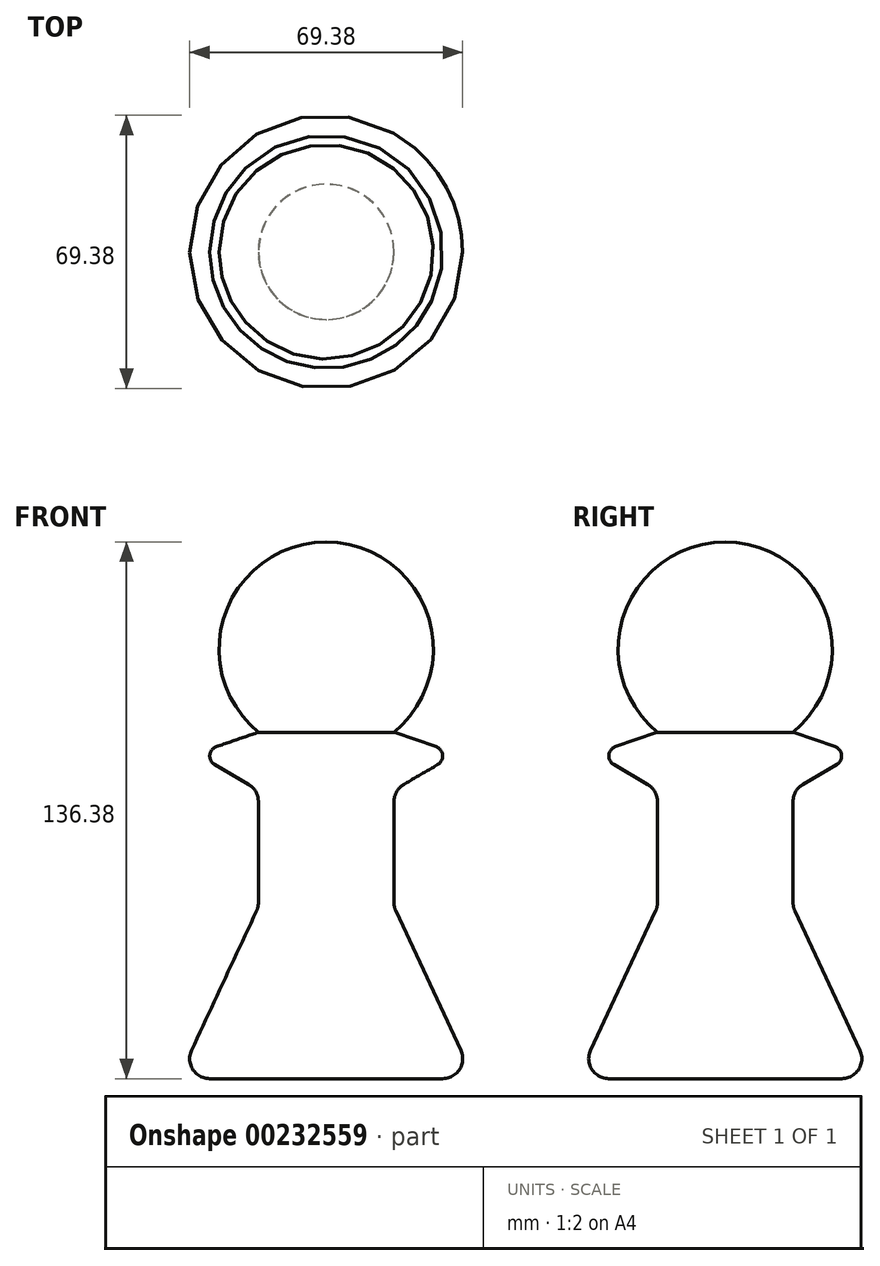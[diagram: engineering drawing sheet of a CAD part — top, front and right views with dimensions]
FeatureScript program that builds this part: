
annotation { "Feature Type Name" : "Feature", "Feature Type Description" : "" }
export const myFeature = defineFeature(function(context is Context, id is Id, definition is map)
    precondition{}
    {
        {
            var Q0;
            Q0=qCreatedBy(makeId("Right.planeOp"),FACE);
            var sketch = newSketch(context, id + "F0", { "sketchPlane" : qUnion([Q0])});
            skLineSegment(sketch, "E0.right", {"start": v(17.23, 14.67) * mm, "end": v(17.23, -73.33) * mm});
            skPoint(sketch, "E1", {"position": v(17.23, -29.74) * mm});
            skPoint(sketch, "E2", {"position": v(17.23, 14.67) * mm});
            skLineSegment(sketch, "E3", {"start": v(17.23, -73.33) * mm, "end": v(37.58, -73.33) * mm});
            skLineSegment(sketch, "E4", {"start": v(17.23, -29.74) * mm, "end": v(37.58, -73.33) * mm});
            skLineSegment(sketch, "E5", {"start": v(17.23, 14.67) * mm, "end": v(33.14, 9.26) * mm});
            skLineSegment(sketch, "E6", {"start": v(33.14, 9.26) * mm, "end": v(17.23, 0) * mm});
            skLineSegment(sketch, "E7", {"start": v(0, 63.05) * mm, "end": v(0, -73.33) * mm});
            skArc(sketch, "E8", {"start": v(0, 8.54) * mm, "mid": v(27.22, 35.8) * mm, "end": v(0, 63.05) * mm});
            skLineSegment(sketch, "E9.bottom", {"start": v(0, 14.67) * mm, "end": v(17.23, 14.67) * mm});
            skLineSegment(sketch, "E9.top", {"start": v(0, -73.33) * mm, "end": v(17.23, -73.33) * mm});
            skLineSegment(sketch, "E9.left", {"start": v(0, 14.67) * mm, "end": v(0, -73.33) * mm});
            skSolve(sketch);
        }
        {
            var Q0;
            {var subQ0=sQuery(id+"F0.wireOp",EDGE,"E3");Q0=makeQuery(id+"F0.imprint","IMPRINT",FACE,{"disambiguationData":[TD([[makeQuery(id+"F0.imprint","IMPRINT",EDGE,{"derivedFrom":subQ0}),1.0]])]});}
            var Q1;
            {var subQ0=sQuery(id+"F0.wireOp",EDGE,"E5");Q1=makeQuery(id+"F0.imprint","IMPRINT",FACE,{"disambiguationData":[TD([[makeQuery(id+"F0.imprint","IMPRINT",EDGE,{"derivedFrom":subQ0}),-1.0]])]});}
            var Q2;
            {var subQ0=sQuery(id+"F0.wireOp",EDGE,"E9.left");var subQ1=sQuery(id+"F0.wireOp",EDGE,"E8");var subQ2=makeQuery(id+"F0.imprint","INTERSECT",VERTEX,{"derivedFrom":[subQ1,subQ0]});Q2=makeQuery(id+"F0.imprint","IMPRINT",FACE,{"disambiguationData":[TD([[makeQuery(id+"F0.imprint","IMPRINT",EDGE,{"disambiguationData":[TD([[subQ2,-1.0]])],"derivedFrom":subQ1}),1.0]])]});}
            var Q3;
            {var subQ3=sQuery(id+"F0.wireOp",EDGE,"E9.top");Q3=makeQuery(id+"F0.imprint","IMPRINT",FACE,{"disambiguationData":[TD([[makeQuery(id+"F0.imprint","IMPRINT",EDGE,{"derivedFrom":subQ3}),1.0]])]});}
            var Q4;
            {var subQ0=sQuery(id+"F0.wireOp",EDGE,"E7");Q4=makeQuery(id+"F0.imprint","IMPRINT",FACE,{"disambiguationData":[TD([[makeQuery(id+"F0.imprint","IMPRINT",EDGE,{"derivedFrom":subQ0}),1.0]])]});}
            var Q5;
            Q5=sQuery(id+"F0.wireOp",EDGE,"E7");
            revolve(context, id + "F1", {"entities" : qUnion([Q0, Q1, Q2, Q3, Q4]), "axis" : qUnion([Q5]), "revolveType" : RevolveType.FULL});
        }
        {
            var Q0;
            Q0=makeQuery(id+"F1.opRevolve","SWEPT_EDGE",EDGE,{"disambiguationData":[OSD([sQuery(id+"F0.wireOp",EDGE,"E5"),sQuery(id+"F0.wireOp",EDGE,"E6")])]});
            fillet(context, id + "F2", {"entities" : qUnion([Q0]), "radius" : 2.54 * mm, "tangentPropagation" : true, "allowEdgeOverflow" : false});
        }
        {
            var Q0;
            Q0=makeQuery(id+"F1.opRevolve","SWEPT_EDGE",EDGE,{"disambiguationData":[OSD([sQuery(id+"F0.wireOp",EDGE,"E5"),sQuery(id+"F0.wireOp",EDGE,"E9.bottom"),sQuery(id+"F0.wireOp",EDGE,"E0.right")])]});
            fillet(context, id + "F3", {"entities" : qUnion([Q0]), "radius" : 5.08 * mm, "tangentPropagation" : true, "allowEdgeOverflow" : false});
        }
        {
            var Q0;
            {var subQ0=sQuery(id+"F0.wireOp",EDGE,"E5");Q0=makeQuery(id+"F3.opFillet","BLEND_EDGE",EDGE,{"blendedFrom":[makeQuery(id+"F1.opRevolve","SWEPT_EDGE",EDGE,{"disambiguationData":[OSD([subQ0,sQuery(id+"F0.wireOp",EDGE,"E9.bottom"),sQuery(id+"F0.wireOp",EDGE,"E0.right")])]}),makeQuery(id+"F1.opRevolve","SWEPT_FACE",FACE,{"disambiguationData":[OSD([subQ0])]})],"blendedInto":[makeQuery(id+"F1.opRevolve","SWEPT_FACE",FACE,{"disambiguationData":[OSD([subQ0])]})]});}
            var Q1;
            Q1=makeQuery(id+"F1.opRevolve","SWEPT_FACE",FACE,{"disambiguationData":[OSD([sQuery(id+"F0.wireOp",EDGE,"E6")])]});
            var Q2;
            Q2=makeQuery(id+"F1.opRevolve","SWEPT_EDGE",EDGE,{"disambiguationData":[OSD([sQuery(id+"F0.wireOp",EDGE,"E4"),sQuery(id+"F0.wireOp",EDGE,"E0.right")])]});
            var Q3;
            Q3=makeQuery(id+"F1.opRevolve","SWEPT_FACE",FACE,{"disambiguationData":[OSD([sQuery(id+"F0.wireOp",EDGE,"E4")])]});
            fillet(context, id + "F4", {"entities" : qUnion([Q0, Q1, Q2, Q3]), "radius" : 5.08 * mm, "tangentPropagation" : true, "allowEdgeOverflow" : false});
        }
    });
